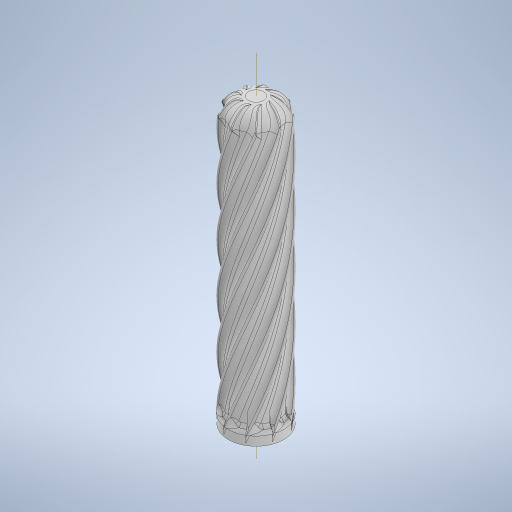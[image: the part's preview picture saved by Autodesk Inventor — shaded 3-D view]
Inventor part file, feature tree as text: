
AUTODESK INVENTOR PART (.ipt)
format: ipt  version: 2023 (Build 270158030, 158C)  size: 2,139,648 bytes
history: native  units: mm
features: fillet x6, sketch x4, projected_geometry x4, extrude x3, helix x1, pattern_circular x1
ambient origin geometry x8: Origin, YZ Plane, XZ Plane, XY Plane, X Axis, Y Axis, Z Axis, Center Point
bodies: Solid1 (feature_tree)
feature tree (19):
  extrude  "Extrusion1"  Depth=71.0mm TaperAngle=0.0deg
  extrude  "Extrusion2"  Depth=7.1mm
  extrude  "Extrusion3"  Depth=3.55mm
  fillet  "Fillet1"  Radius=13.2mm
  helix  "Coil1"  [1 undecoded]
  fillet  "Fillet3"  Radius=68.0mm
  fillet  "Fillet2"  Radius=2.4mm
  fillet  "Fillet10"  Radius=1.2mm
  pattern_circular  "Circular Pattern1"  [2 undecoded]
  fillet  "Fillet8"  Radius=1.0mm
  fillet  "Fillet9"  Radius=90.0mm
  sketch  "Sketch1"  dims[d0=13.85mm d1=71.0mm d2=0.0mm]
  sketch  "Sketch2"  dims[d3=7.1mm d4=7.1mm]
  sketch  "Sketch3"  dims[d5=3.55mm d6=3.55mm d7=13.2mm d8=0.0mm d9=11.6mm d10=68.0mm d11=0.0mm d12=2.4mm d13=1.2mm]
  projected_geometry  "Projected Loop1"
  sketch  "Sketch4"  dims[d14=70.0mm d15=66.0mm d16=6.0mm d17=0.0mm d18=90.0deg d19=90.0deg d20=0.0mm d21=0.174533mm d22=3.9mm d23=1.7mm d24=1.0mm d26=90.0mm d27=360.0deg d32=1.0mm d33=0.16mm d34=1.7mm]
  projected_geometry  "Projected Loop2"
  projected_geometry  "Projected Loop3"
  projected_geometry  "Projected Loop4"
note: 3 required parameter values undecoded (feature->parameter linkage not recoverable at this tier; creation-order binding heuristic only, values carry confidence <= 0.55)
